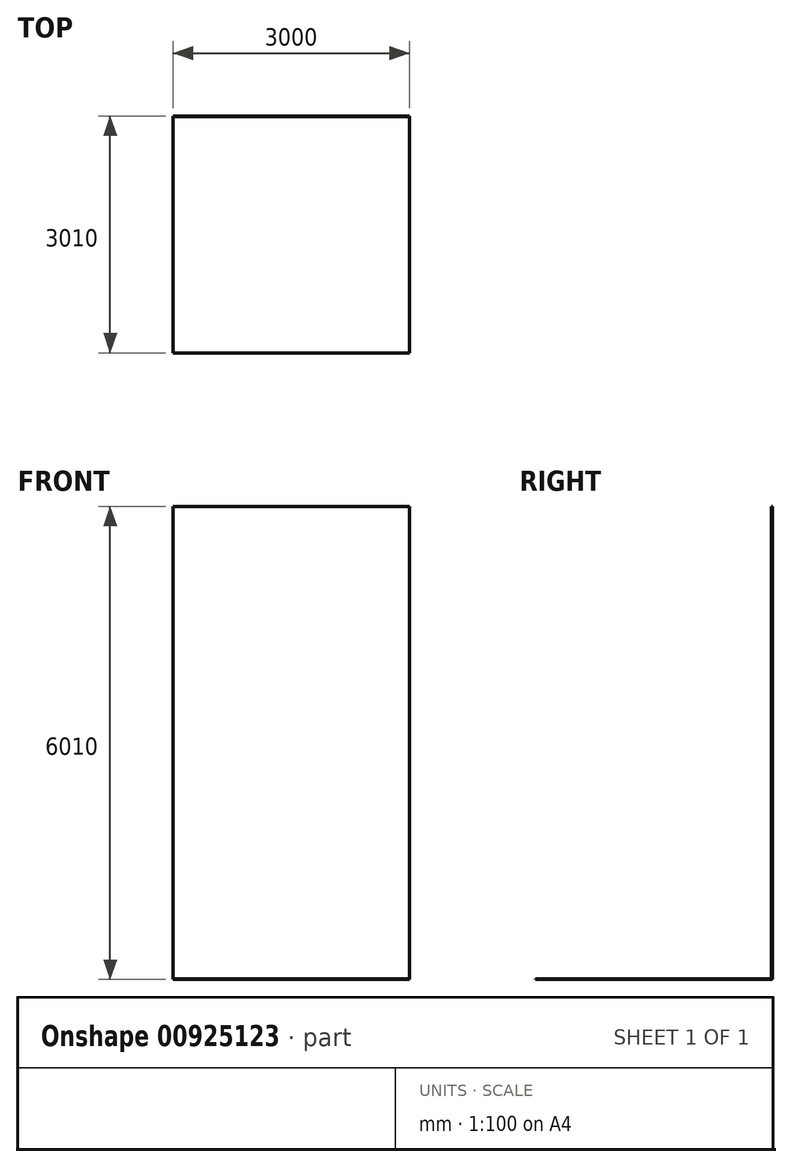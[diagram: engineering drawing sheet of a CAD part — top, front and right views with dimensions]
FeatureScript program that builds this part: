
annotation { "Feature Type Name" : "Feature", "Feature Type Description" : "" }
export const myFeature = defineFeature(function(context is Context, id is Id, definition is map)
    precondition{}
    {
        {
            var Q0;
            Q0=qCreatedBy(makeId("Right.planeOp"),FACE);
            var sketch = newSketch(context, id + "F0", { "sketchPlane" : qUnion([Q0])});
            skLineSegment(sketch, "E0", {"start": v(0, 0) * mm, "end": v(0, 6000) * mm});
            skLineSegment(sketch, "E1", {"start": v(0, 0) * mm, "end": v(-3000, 0) * mm});
            skLineSegment(sketch, "E2.0", {"start": v(10, -10) * mm, "end": v(-3000, -10) * mm});
            skLineSegment(sketch, "E2.1", {"start": v(10, -10) * mm, "end": v(10, 6000) * mm});
            skLineSegment(sketch, "E3", {"start": v(-3000, 0) * mm, "end": v(-3000, -10) * mm});
            skLineSegment(sketch, "E4", {"start": v(10, 6000) * mm, "end": v(0, 6000) * mm});
            skSolve(sketch);
        }
        {
            var Q0;
            Q0 = qSketchRegion(id + "F0", true);
            extrude(context, id + "F1", {"entities" : qUnion([Q0]), "endBound" : BoundingType.SYMMETRIC, "depth" : 3000 * mm, "offsetDistance" : 25 * mm});
        }
    });
